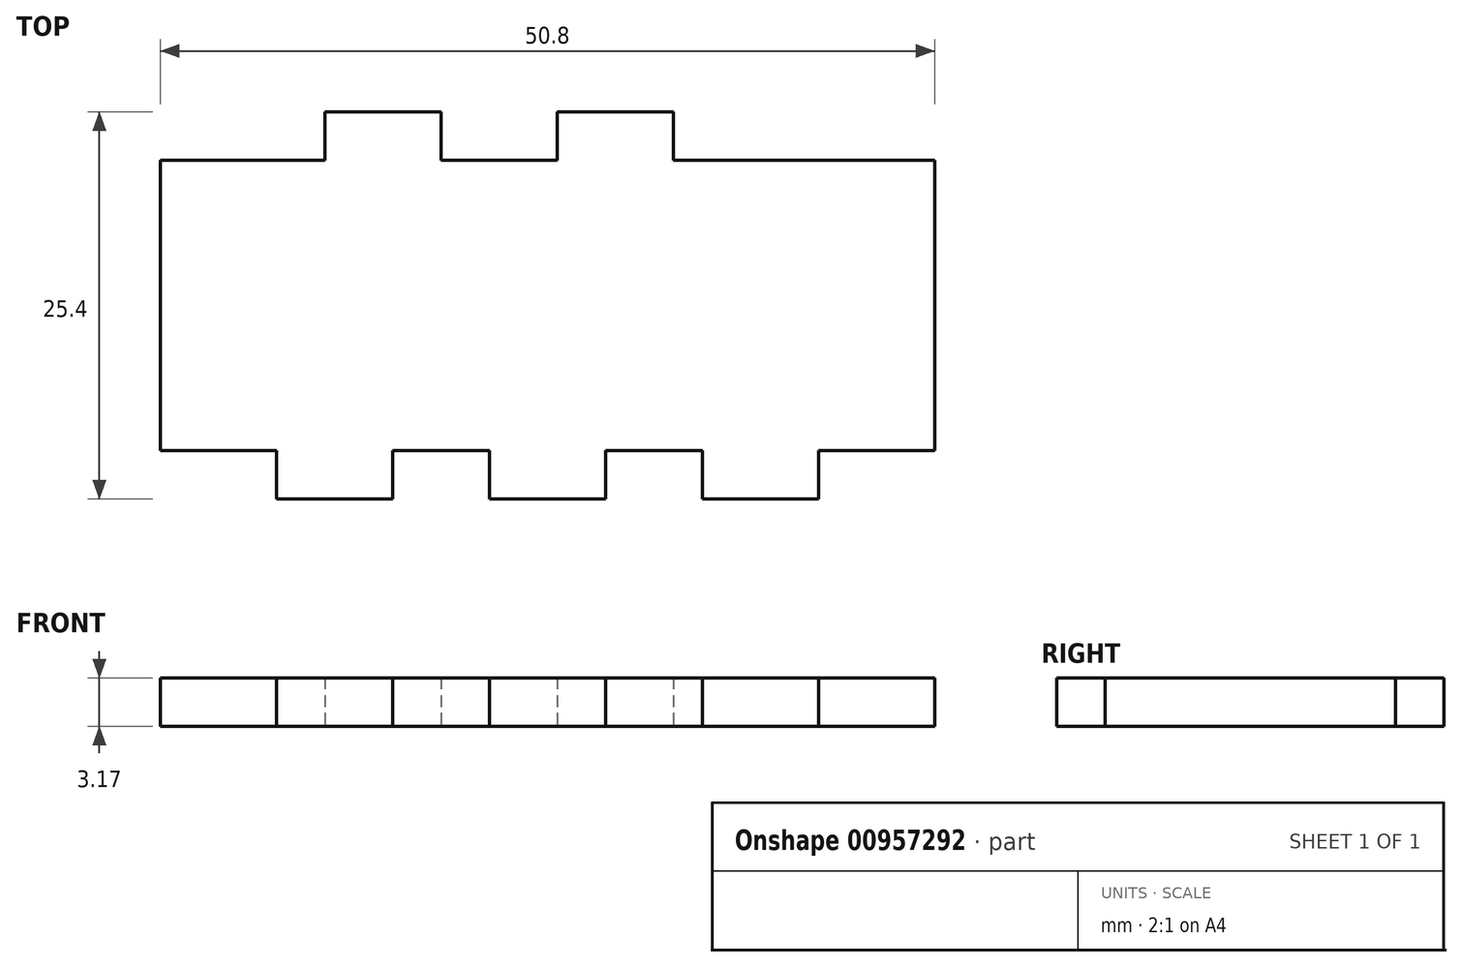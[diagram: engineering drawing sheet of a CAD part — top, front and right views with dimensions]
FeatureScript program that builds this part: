
annotation { "Feature Type Name" : "Feature", "Feature Type Description" : "" }
export const myFeature = defineFeature(function(context is Context, id is Id, definition is map)
    precondition{}
    {
        {
            var Q0;
            Q0=qCreatedBy(makeId("Top.planeOp"),FACE);
            var sketch = newSketch(context, id + "F0", { "sketchPlane" : qUnion([Q0])});
            skLineSegment(sketch, "E0", {"start": v(0, 0) * mm, "end": v(7.62, 0) * mm});
            skLineSegment(sketch, "E1", {"start": v(7.62, 0) * mm, "end": v(7.62, -12.7) * mm});
            skLineSegment(sketch, "E2", {"start": v(7.62, -12.7) * mm, "end": v(15.24, -12.7) * mm});
            skLineSegment(sketch, "E3", {"start": v(15.24, -12.7) * mm, "end": v(15.24, 0) * mm});
            skLineSegment(sketch, "E4", {"start": v(15.24, 0) * mm, "end": v(21.59, 0) * mm});
            skLineSegment(sketch, "E5", {"start": v(21.59, 0) * mm, "end": v(21.59, -12.7) * mm});
            skLineSegment(sketch, "E6", {"start": v(21.59, -12.7) * mm, "end": v(29.2, -12.7) * mm});
            skLineSegment(sketch, "E7", {"start": v(29.21, -12.7) * mm, "end": v(29.21, 0) * mm});
            skLineSegment(sketch, "E8", {"start": v(29.21, 0) * mm, "end": v(35.56, 0) * mm});
            skLineSegment(sketch, "E9", {"start": v(35.56, 0) * mm, "end": v(35.56, -12.7) * mm});
            skLineSegment(sketch, "E10", {"start": v(35.56, -12.7) * mm, "end": v(43.18, -12.7) * mm});
            skLineSegment(sketch, "E11", {"start": v(43.18, -12.7) * mm, "end": v(43.18, 0) * mm});
            skLineSegment(sketch, "E12", {"start": v(43.18, 0) * mm, "end": v(50.8, 0) * mm});
            skLineSegment(sketch, "E13", {"start": v(50.8, 0) * mm, "end": v(50.8, 12.7) * mm});
            skLineSegment(sketch, "E14", {"start": v(50.8, 12.7) * mm, "end": v(33.65, 12.7) * mm});
            skLineSegment(sketch, "E15", {"start": v(33.65, 12.7) * mm, "end": v(33.65, 25.4) * mm});
            skLineSegment(sketch, "E16", {"start": v(33.65, 25.4) * mm, "end": v(26.03, 25.4) * mm});
            skLineSegment(sketch, "E17", {"start": v(26.03, 25.4) * mm, "end": v(26.03, 12.7) * mm});
            skLineSegment(sketch, "E18", {"start": v(26.03, 12.7) * mm, "end": v(18.41, 12.7) * mm});
            skLineSegment(sketch, "E19", {"start": v(18.41, 12.7) * mm, "end": v(18.41, 25.4) * mm});
            skLineSegment(sketch, "E20", {"start": v(18.41, 25.4) * mm, "end": v(10.8, 25.4) * mm});
            skLineSegment(sketch, "E21", {"start": v(10.8, 25.4) * mm, "end": v(10.8, 12.7) * mm});
            skLineSegment(sketch, "E22", {"start": v(10.8, 12.7) * mm, "end": v(0, 12.7) * mm});
            skLineSegment(sketch, "E23", {"start": v(0, 12.7) * mm, "end": v(0, 0) * mm});
            skSolve(sketch);
        }
        {
            var Q0;
            Q0=makeQuery(id+"F0.imprint","IMPRINT",FACE,{"disambiguationData":[TD([[makeQuery(id+"F0.imprint","IMPRINT",EDGE,{"derivedFrom":sQuery(id+"F0.wireOp",EDGE,"E0")}),1.0]])]});
            extrude(context, id + "F1", {"entities" : qUnion([Q0]), "depth" : 3.17 * mm, "offsetDistance" : 25.4 * mm});
        }
        {
            var Q0;
            Q0=makeQuery(id+"F1.opExtrude","SWEPT_FACE",FACE,{"disambiguationData":[OSD([sQuery(id+"F0.wireOp",EDGE,"E20")])]});
            var Q1;
            Q1=makeQuery(id+"F1.opExtrude","SWEPT_FACE",FACE,{"disambiguationData":[OSD([sQuery(id+"F0.wireOp",EDGE,"E16")])]});
            extrude(context, id + "F2", {"entities" : qUnion([Q0, Q1]), "operationType" : NewBodyOperationType.REMOVE, "oppositeDirection" : true, "depth" : 9.52 * mm, "offsetDistance" : 25.4 * mm});
        }
        {
            var Q0;
            Q0=makeQuery(id+"F1.opExtrude","SWEPT_FACE",FACE,{"disambiguationData":[OSD([sQuery(id+"F0.wireOp",EDGE,"E10")])]});
            var Q1;
            Q1=makeQuery(id+"F1.opExtrude","SWEPT_FACE",FACE,{"disambiguationData":[OSD([sQuery(id+"F0.wireOp",EDGE,"E6")])]});
            var Q2;
            Q2=makeQuery(id+"F1.opExtrude","SWEPT_FACE",FACE,{"disambiguationData":[OSD([sQuery(id+"F0.wireOp",EDGE,"E2")])]});
            extrude(context, id + "F3", {"entities" : qUnion([Q0, Q1, Q2]), "operationType" : NewBodyOperationType.REMOVE, "oppositeDirection" : true, "depth" : 9.52 * mm, "offsetDistance" : 25.4 * mm});
        }
        {
            var Q0;
            Q0=makeQuery(id+"F1.opExtrude","SWEPT_FACE",FACE,{"disambiguationData":[OSD([sQuery(id+"F0.wireOp",EDGE,"E14")])]});
            var Q1;
            Q1=makeQuery(id+"F2.boolean.opBoolean","COPY",FACE,{"derivedFrom":makeQuery(id+"F2.opExtrude","CAP_FACE",FACE,{"disambiguationData":[OSD([sQuery(id+"F0.wireOp",EDGE,"E16")])],"isStart":false})});
            var Q2;
            Q2=makeQuery(id+"F1.opExtrude","SWEPT_FACE",FACE,{"disambiguationData":[OSD([sQuery(id+"F0.wireOp",EDGE,"E18")])]});
            var Q3;
            Q3=makeQuery(id+"F2.boolean.opBoolean","COPY",FACE,{"derivedFrom":makeQuery(id+"F2.opExtrude","CAP_FACE",FACE,{"disambiguationData":[OSD([sQuery(id+"F0.wireOp",EDGE,"E20")])],"isStart":false})});
            var Q4;
            Q4=makeQuery(id+"F1.opExtrude","SWEPT_FACE",FACE,{"disambiguationData":[OSD([sQuery(id+"F0.wireOp",EDGE,"E22")])]});
            extrude(context, id + "F4", {"entities" : qUnion([Q0, Q1, Q2, Q3, Q4]), "operationType" : NewBodyOperationType.ADD, "depth" : 6.35 * mm, "offsetDistance" : 25.4 * mm});
        }
    });
